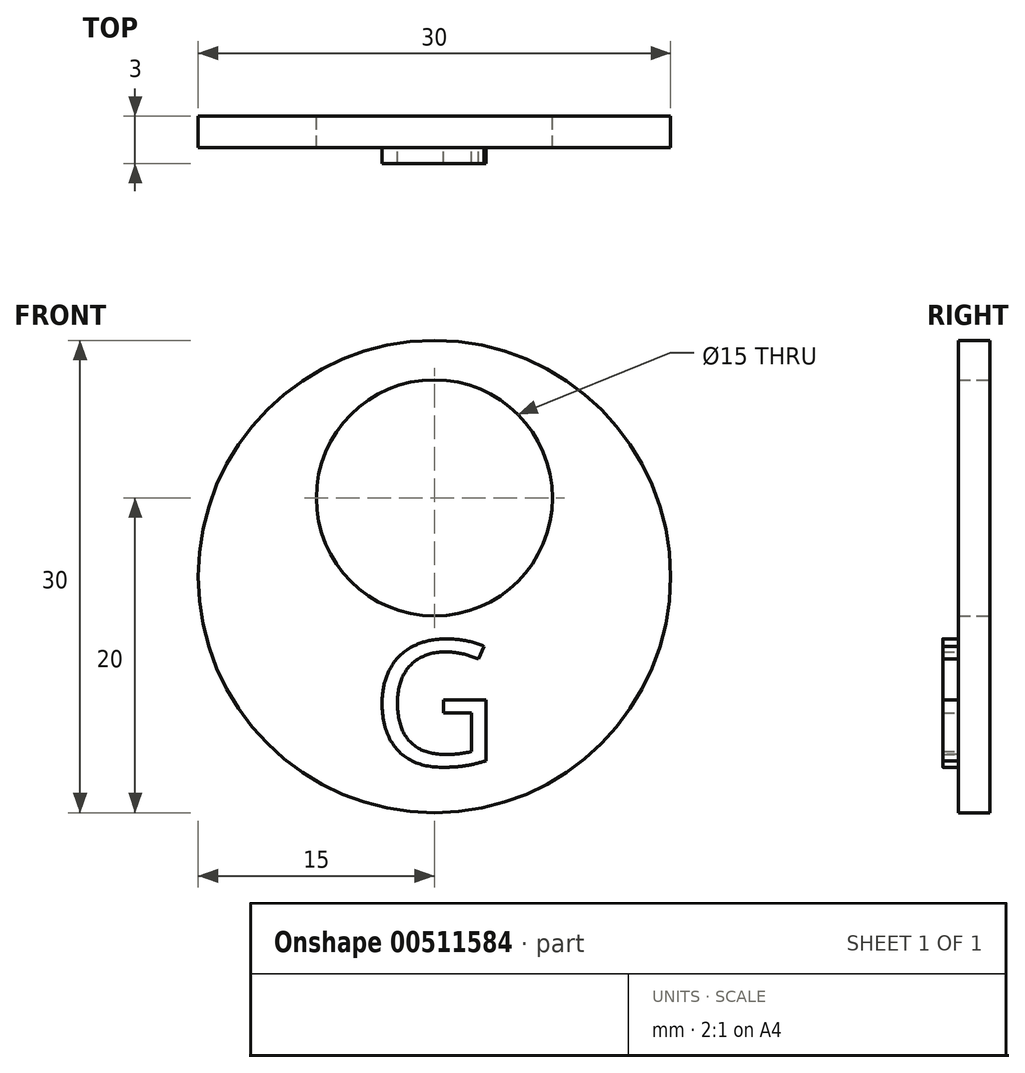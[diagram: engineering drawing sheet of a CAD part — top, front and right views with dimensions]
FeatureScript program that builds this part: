
annotation { "Feature Type Name" : "Feature", "Feature Type Description" : "" }
export const myFeature = defineFeature(function(context is Context, id is Id, definition is map)
    precondition{}
    {
        {
            var Q0;
            Q0=qCreatedBy(makeId("Front.planeOp"),FACE);
            var sketch = newSketch(context, id + "F0", { "sketchPlane" : qUnion([Q0])});
            skCircle(sketch, "E0", {"center": v(0, 0) * mm, "radius": 15 * mm});
            skPoint(sketch, "E1", {"position": v(0, 5) * mm});
            skCircle(sketch, "E2", {"center": v(0, 5) * mm, "radius": 7.5 * mm});
            skSolve(sketch);
        }
        {
            var Q0;
            Q0=makeQuery(id+"F0.imprint","IMPRINT",FACE,{"disambiguationData":[TD([[makeQuery(id+"F0.imprint","IMPRINT",EDGE,{"derivedFrom":sQuery(id+"F0.wireOp",EDGE,"E0")}),1.0]])]});
            extrude(context, id + "F1", {"entities" : qUnion([Q0]), "depth" : 2 * mm});
        }
        {
            var Q0;
            Q0=makeQuery(id+"F1.opExtrude","CAP_FACE",FACE,{"disambiguationData":[OSD([sQuery(id+"F0.wireOp",EDGE,"E0"),sQuery(id+"F0.wireOp",EDGE,"E2")])],"isStart":false});
            var sketch = newSketch(context, id + "F2", { "sketchPlane" : qUnion([Q0])});
            skText(sketch, "E3", { "text": "G", "fontName": "OpenSans-Regular.ttf"});
            const initialGuessF2  = {"E3": [-0.004, -0.012, 1, 0, 0.008]};
            skSetInitialGuess(sketch, initialGuessF2);
            skSolve(sketch);
        }
        {
            var Q0;
            Q0=qSketchRegion(id+"F2",true);
            extrude(context, id + "F3", {"entities" : qUnion([Q0]), "operationType" : NewBodyOperationType.ADD, "depth" : 1 * mm});
        }
    });
